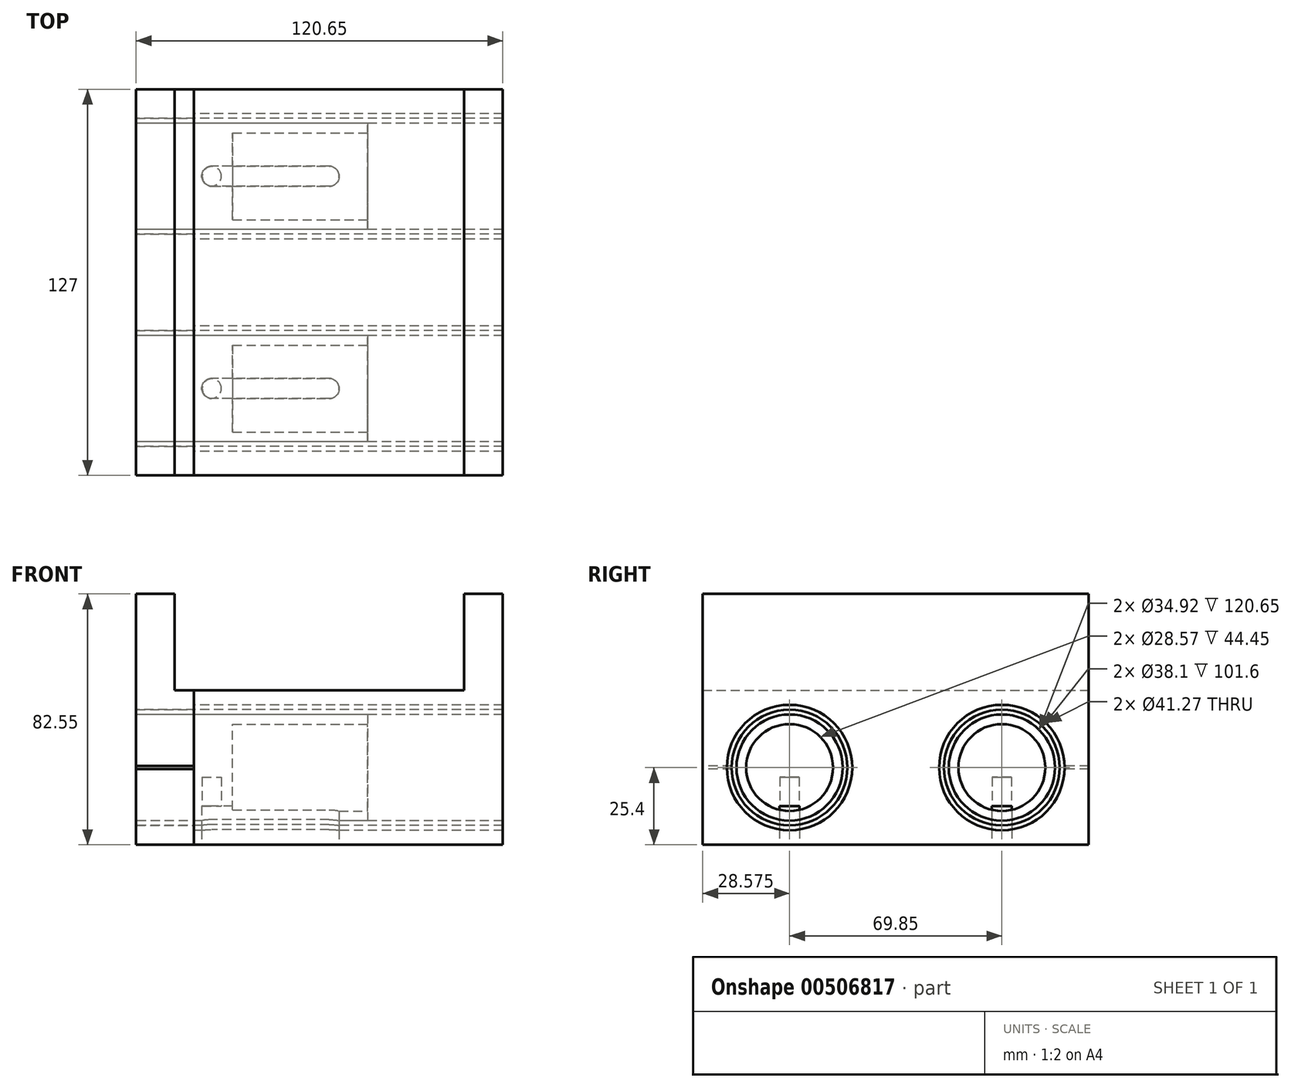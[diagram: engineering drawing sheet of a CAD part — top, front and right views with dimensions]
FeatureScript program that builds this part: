
annotation { "Feature Type Name" : "Feature", "Feature Type Description" : "" }
export const myFeature = defineFeature(function(context is Context, id is Id, definition is map)
    precondition{}
    {
        {
            var Q0;
            Q0=qCreatedBy(makeId("Right.planeOp"),FACE);
            var sketch = newSketch(context, id + "F0", { "sketchPlane" : qUnion([Q0])});
            skLineSegment(sketch, "E0.bottom", {"start": v(0, 0) * mm, "end": v(127, 0) * mm});
            skLineSegment(sketch, "E0.top", {"start": v(0, 50.8) * mm, "end": v(127, 50.8) * mm});
            skLineSegment(sketch, "E0.left", {"start": v(0, 0) * mm, "end": v(0, 50.8) * mm});
            skLineSegment(sketch, "E0.right", {"start": v(127, 0) * mm, "end": v(127, 50.8) * mm});
            skCircle(sketch, "E1", {"center": v(28.57, 25.4) * mm, "radius": 20.64 * mm});
            skCircle(sketch, "E2", {"center": v(98.43, 25.4) * mm, "radius": 20.64 * mm});
            skLineSegment(sketch, "E3", {"start": v(0, 25.4) * mm, "end": v(7.94, 25.4) * mm, "construction": true});
            skLineSegment(sketch, "E4.trimOffspring", {"start": v(28.57, 25.4) * mm, "end": v(98.43, 25.4) * mm, "construction": true});
            skLineSegment(sketch, "E5.trimOffspring", {"start": v(119.06, 25.4) * mm, "end": v(127, 25.4) * mm, "construction": true});
            skSolve(sketch);
        }
        {
            var Q0;
            Q0 = qSketchRegion(id + "F0", true);
            extrude(context, id + "F1", {"entities" : qUnion([Q0]), "depth" : 88.9 * mm, "offsetDistance" : 25.4 * mm});
        }
        {
            var Q0;
            Q0=makeQuery(id+"F1.opExtrude","CAP_FACE",FACE,{"disambiguationData":[OSD([sQuery(id+"F0.wireOp",EDGE,"E0.bottom"),sQuery(id+"F0.wireOp",EDGE,"E0.top"),sQuery(id+"F0.wireOp",EDGE,"E0.left"),sQuery(id+"F0.wireOp",EDGE,"E0.right"),sQuery(id+"F0.wireOp",EDGE,"E1"),sQuery(id+"F0.wireOp",EDGE,"E2")])],"isStart":true});
            var sketch = newSketch(context, id + "F2", { "sketchPlane" : qUnion([Q0])});
            skCircle(sketch, "E6", {"center": v(-98.43, 25.4) * mm, "radius": 20.64 * mm});
            skCircle(sketch, "E7", {"center": v(-28.57, 25.4) * mm, "radius": 20.64 * mm});
            skCircle(sketch, "E8", {"center": v(-98.43, 25.4) * mm, "radius": 19.05 * mm});
            skCircle(sketch, "E9", {"center": v(-28.57, 25.4) * mm, "radius": 19.05 * mm});
            skSolve(sketch);
        }
        {
            var Q0;
            Q0 = qSketchRegion(id + "F2", true);
            extrude(context, id + "F3", {"entities" : qUnion([Q0]), "oppositeDirection" : true, "depth" : 101.6 * mm, "offsetDistance" : 25.4 * mm});
        }
        {
            var Q0;
            Q0=makeQuery(id+"F1.opExtrude","CAP_FACE",FACE,{"disambiguationData":[OSD([sQuery(id+"F0.wireOp",EDGE,"E0.bottom"),sQuery(id+"F0.wireOp",EDGE,"E0.top"),sQuery(id+"F0.wireOp",EDGE,"E0.left"),sQuery(id+"F0.wireOp",EDGE,"E0.right"),sQuery(id+"F0.wireOp",EDGE,"E1"),sQuery(id+"F0.wireOp",EDGE,"E2")])],"isStart":false});
            extrude(context, id + "F4", {"entities" : qUnion([Q0]), "depth" : 12.7 * mm, "offsetDistance" : 25.4 * mm});
        }
        {
            var Q0;
            Q0=makeQuery(id+"F4.opExtrude","SWEPT_FACE",FACE,{"disambiguationData":[OSD([sQuery(id+"F0.wireOp",EDGE,"E0.top")])]});
            extrude(context, id + "F5", {"entities" : qUnion([Q0]), "operationType" : NewBodyOperationType.ADD, "depth" : 31.75 * mm, "offsetDistance" : 25.4 * mm});
        }
        {
            var Q0;
            Q0=makeQuery(id+"F1.opExtrude","CAP_FACE",FACE,{"disambiguationData":[OSD([sQuery(id+"F0.wireOp",EDGE,"E0.bottom"),sQuery(id+"F0.wireOp",EDGE,"E0.top"),sQuery(id+"F0.wireOp",EDGE,"E0.left"),sQuery(id+"F0.wireOp",EDGE,"E0.right"),sQuery(id+"F0.wireOp",EDGE,"E1"),sQuery(id+"F0.wireOp",EDGE,"E2")])],"isStart":true});
            var sketch = newSketch(context, id + "F6", { "sketchPlane" : qUnion([Q0])});
            skCircle(sketch, "E10", {"center": v(-98.43, 25.4) * mm, "radius": 19.05 * mm});
            skCircle(sketch, "E11", {"center": v(-28.57, 25.4) * mm, "radius": 19.05 * mm});
            skCircle(sketch, "E12", {"center": v(-98.43, 25.4) * mm, "radius": 17.46 * mm});
            skCircle(sketch, "E13", {"center": v(-28.57, 25.4) * mm, "radius": 17.46 * mm});
            skSolve(sketch);
        }
        {
            var Q0;
            Q0 = qSketchRegion(id + "F6", true);
            extrude(context, id + "F7", {"entities" : qUnion([Q0]), "oppositeDirection" : true, "depth" : 101.6 * mm, "offsetDistance" : 25.4 * mm, "hasSecondDirection" : true, "secondDirectionOppositeDirection" : false, "secondDirectionDepth" : 19.05 * mm});
        }
        {
            var Q0;
            Q0=makeQuery(id+"F1.opExtrude","CAP_FACE",FACE,{"disambiguationData":[OSD([sQuery(id+"F0.wireOp",EDGE,"E0.bottom"),sQuery(id+"F0.wireOp",EDGE,"E0.top"),sQuery(id+"F0.wireOp",EDGE,"E0.left"),sQuery(id+"F0.wireOp",EDGE,"E0.right"),sQuery(id+"F0.wireOp",EDGE,"E1"),sQuery(id+"F0.wireOp",EDGE,"E2")])],"isStart":true});
            var sketch = newSketch(context, id + "F8", { "sketchPlane" : qUnion([Q0])});
            skLineSegment(sketch, "E14.bottom", {"start": v(-127, 0) * mm, "end": v(0, 0) * mm});
            skLineSegment(sketch, "E14.top", {"start": v(-127, 82.55) * mm, "end": v(0, 82.55) * mm});
            skLineSegment(sketch, "E14.left", {"start": v(-127, 0) * mm, "end": v(-127, 24.9) * mm});
            skLineSegment(sketch, "E14.right", {"start": v(0, 0) * mm, "end": v(0, 24.9) * mm});
            skArc(sketch, "E15", {"start": v(-117.47, 24.9) * mm, "mid": v(-79.38, 25.4) * mm, "end": v(-117.47, 25.9) * mm});
            skArc(sketch, "E16", {"start": v(-9.52, 25.4) * mm, "mid": v(-47.62, 25.65) * mm, "end": v(-9.53, 24.9) * mm});
            skLineSegment(sketch, "E17", {"start": v(-127, 25.4) * mm, "end": v(0, 25.4) * mm, "construction": true});
            skLineSegment(sketch, "E18.0", {"start": v(-127, 24.9) * mm, "end": v(-117.47, 24.9) * mm});
            skLineSegment(sketch, "E19.0", {"start": v(-127, 25.9) * mm, "end": v(-117.47, 25.9) * mm});
            skLineSegment(sketch, "E20.trimOffspring", {"start": v(-9.53, 25.9) * mm, "end": v(0, 25.9) * mm});
            skLineSegment(sketch, "E21.trimOffspring", {"start": v(-9.53, 24.9) * mm, "end": v(0, 24.9) * mm});
            skLineSegment(sketch, "E22.trimOffspring", {"start": v(0, 25.9) * mm, "end": v(0, 82.55) * mm});
            skLineSegment(sketch, "E23.trimOffspring", {"start": v(-127, 25.9) * mm, "end": v(-127, 82.55) * mm});
            skSolve(sketch);
        }
        {
            var Q0;
            Q0 = qSketchRegion(id + "F8", true);
            extrude(context, id + "F9", {"entities" : qUnion([Q0]), "depth" : 19.05 * mm, "offsetDistance" : 25.4 * mm});
        }
        {
            var Q0;
            Q0=makeQuery(id+"F9.opExtrude","SWEPT_FACE",FACE,{"disambiguationData":[OSD([sQuery(id+"F8.wireOp",EDGE,"E14.top")])]});
            var sketch = newSketch(context, id + "F10", { "sketchPlane" : qUnion([Q0])});
            skLineSegment(sketch, "E24", {"start": v(-6.35, 127) * mm, "end": v(-6.35, 0) * mm});
            skLineSegment(sketch, "E25", {"start": v(-6.35, 0) * mm, "end": v(0, 0) * mm});
            skLineSegment(sketch, "E26", {"start": v(0, 0) * mm, "end": v(0, 127) * mm});
            skLineSegment(sketch, "E27", {"start": v(0, 127) * mm, "end": v(-6.35, 127) * mm});
            skSolve(sketch);
        }
        {
            var Q0;
            Q0 = qSketchRegion(id + "F10", true);
            extrude(context, id + "F11", {"entities" : qUnion([Q0]), "operationType" : NewBodyOperationType.REMOVE, "oppositeDirection" : true, "depth" : 31.75 * mm, "offsetDistance" : 25.4 * mm});
        }
        {
            var Q0;
            Q0=makeQuery(id+"F9.opExtrude","CAP_FACE",FACE,{"disambiguationData":[OSD([sQuery(id+"F8.wireOp",EDGE,"E14.bottom"),sQuery(id+"F8.wireOp",EDGE,"E14.top"),sQuery(id+"F8.wireOp",EDGE,"E14.left"),sQuery(id+"F8.wireOp",EDGE,"E14.right"),sQuery(id+"F8.wireOp",EDGE,"E15"),sQuery(id+"F8.wireOp",EDGE,"E16"),sQuery(id+"F8.wireOp",EDGE,"E18.0"),sQuery(id+"F8.wireOp",EDGE,"E19.0"),sQuery(id+"F8.wireOp",EDGE,"E20.trimOffspring"),sQuery(id+"F8.wireOp",EDGE,"E21.trimOffspring"),sQuery(id+"F8.wireOp",EDGE,"E22.trimOffspring"),sQuery(id+"F8.wireOp",EDGE,"E23.trimOffspring")])],"isStart":false});
            var sketch = newSketch(context, id + "F12", { "sketchPlane" : qUnion([Q0])});
            skCircle(sketch, "E28", {"center": v(-98.43, 25.4) * mm, "radius": 17.46 * mm});
            skCircle(sketch, "E29", {"center": v(-28.57, 25.4) * mm, "radius": 17.46 * mm});
            skSolve(sketch);
        }
        {
            var Q0;
            Q0 = qSketchRegion(id + "F12", true);
            extrude(context, id + "F13", {"entities" : qUnion([Q0]), "oppositeDirection" : true, "depth" : 76.2 * mm, "offsetDistance" : 25.4 * mm});
        }
        {
            var Q0;
            Q0=makeQuery(id+"F1.opExtrude","SWEPT_FACE",FACE,{"disambiguationData":[OSD([sQuery(id+"F0.wireOp",EDGE,"E0.bottom")])]});
            var sketch = newSketch(context, id + "F14", { "sketchPlane" : qUnion([Q0])});
            skLineSegment(sketch, "E30", {"start": v(88.9, -28.57) * mm, "end": v(0, -28.57) * mm, "construction": true});
            skLineSegment(sketch, "E31", {"start": v(88.9, -98.43) * mm, "end": v(0, -98.43) * mm, "construction": true});
            skLineSegment(sketch, "E32", {"start": v(44.45, -127) * mm, "end": v(44.45, -98.43) * mm, "construction": true});
            skLineSegment(sketch, "E33", {"start": v(44.45, 0) * mm, "end": v(44.45, -28.57) * mm, "construction": true});
            skArc(sketch, "E34", {"start": v(44.45, -31.88) * mm, "mid": v(47.75, -28.57) * mm, "end": v(44.45, -25.27) * mm});
            skArc(sketch, "E35", {"start": v(44.45, -101.73) * mm, "mid": v(47.75, -98.43) * mm, "end": v(44.45, -95.12) * mm});
            skLineSegment(sketch, "E36", {"start": v(44.45, -28.57) * mm, "end": v(44.45, -98.43) * mm, "construction": true});
            skArc(sketch, "E37", {"start": v(5.84, -25.27) * mm, "mid": v(2.54, -28.57) * mm, "end": v(5.84, -31.88) * mm});
            skArc(sketch, "E38", {"start": v(5.84, -95.12) * mm, "mid": v(2.54, -98.43) * mm, "end": v(5.84, -101.73) * mm});
            skLineSegment(sketch, "E39", {"start": v(44.45, -25.27) * mm, "end": v(5.84, -25.27) * mm});
            skLineSegment(sketch, "E40", {"start": v(44.45, -31.88) * mm, "end": v(5.84, -31.88) * mm});
            skLineSegment(sketch, "E41", {"start": v(5.84, -95.12) * mm, "end": v(44.45, -95.12) * mm});
            skLineSegment(sketch, "E42", {"start": v(44.45, -101.73) * mm, "end": v(5.84, -101.73) * mm});
            skSolve(sketch);
        }
        {
            var Q0;
            Q0 = qSketchRegion(id + "F14", true);
            extrude(context, id + "F15", {"entities" : qUnion([Q0]), "operationType" : NewBodyOperationType.REMOVE, "oppositeDirection" : true, "depth" : 12.7 * mm, "offsetDistance" : 25.4 * mm});
        }
        {
            var Q0;
            Q0=makeQuery(id+"F1.opExtrude","SWEPT_FACE",FACE,{"disambiguationData":[OSD([sQuery(id+"F0.wireOp",EDGE,"E0.bottom")])]});
            var sketch = newSketch(context, id + "F16", { "sketchPlane" : qUnion([Q0])});
            skCircle(sketch, "E43", {"center": v(5.84, -98.43) * mm, "radius": 3.18 * mm});
            skCircle(sketch, "E44", {"center": v(5.84, -28.57) * mm, "radius": 3.18 * mm});
            skSolve(sketch);
        }
        {
            var Q0;
            Q0 = qSketchRegion(id + "F16", true);
            extrude(context, id + "F17", {"entities" : qUnion([Q0]), "operationType" : NewBodyOperationType.REMOVE, "oppositeDirection" : true, "depth" : 22.22 * mm, "offsetDistance" : 25.4 * mm});
        }
        {
            var Q0;
            Q0=makeQuery(id+"F13.opExtrude","CAP_FACE",FACE,{"disambiguationData":[OSD([sQuery(id+"F12.wireOp",EDGE,"E28")])],"isStart":false});
            var sketch = newSketch(context, id + "F18", { "sketchPlane" : qUnion([Q0])});
            skCircle(sketch, "E45", {"center": v(98.43, 25.4) * mm, "radius": 14.29 * mm});
            skCircle(sketch, "E46", {"center": v(28.57, 25.4) * mm, "radius": 14.29 * mm});
            skSolve(sketch);
        }
        {
            var Q0;
            Q0 = qSketchRegion(id + "F18", true);
            extrude(context, id + "F19", {"entities" : qUnion([Q0]), "operationType" : NewBodyOperationType.REMOVE, "oppositeDirection" : true, "depth" : 44.45 * mm, "offsetDistance" : 25.4 * mm});
        }
    });
